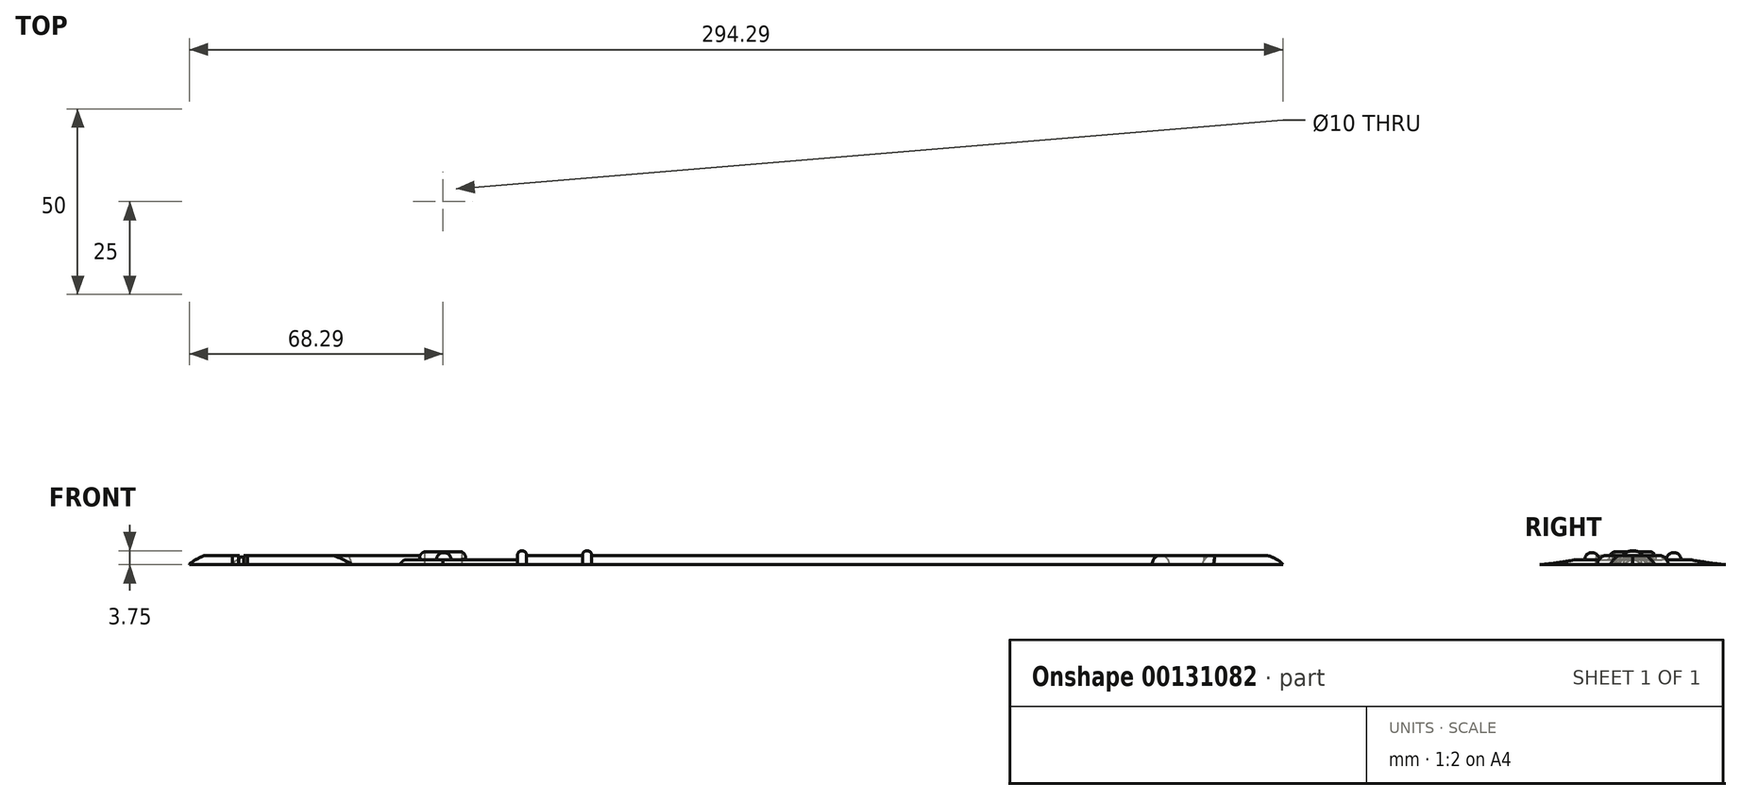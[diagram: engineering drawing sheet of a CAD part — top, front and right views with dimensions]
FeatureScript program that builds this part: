
annotation { "Feature Type Name" : "Feature", "Feature Type Description" : "" }
export const myFeature = defineFeature(function(context is Context, id is Id, definition is map)
    precondition{}
    {
        {
            var Q0;
            Q0=qCreatedBy(makeId("Front.planeOp"),FACE);
            var sketch = newSketch(context, id + "F0", { "sketchPlane" : qUnion([Q0])});
            skLineSegment(sketch, "E0", {"start": v(0, 0) * mm, "end": v(7, 0) * mm});
            skLineSegment(sketch, "E1", {"start": v(7, 0) * mm, "end": v(7, 2.5) * mm});
            skLineSegment(sketch, "E2", {"start": v(0, 0) * mm, "end": v(0, 7) * mm});
            skLineSegment(sketch, "E3", {"start": v(7, 0) * mm, "end": v(9.5, 0) * mm});
            skArc(sketch, "E4", {"start": v(9.5, 0) * mm, "mid": v(7, 2.5) * mm, "end": v(4.5, 0) * mm});
            skSolve(sketch);
        }
        {
            var Q0;
            Q0 = qSketchRegion(id + "F0", true);
            var Q1;
            Q1=sQuery(id+"F0.wireOp",EDGE,"E2");
            revolve(context, id + "F1", {"entities" : qUnion([Q0]), "axis" : qUnion([Q1]), "revolveType" : RevolveType.FULL});
        }
        {
            var Q0;
            Q0=qCreatedBy(makeId("Top.planeOp"),FACE);
            var sketch = newSketch(context, id + "F2", { "sketchPlane" : qUnion([Q0])});
            skLineSegment(sketch, "E5", {"start": v(0, 0) * mm, "end": v(-9, 0) * mm});
            skLineSegment(sketch, "E6", {"start": v(-9, 0) * mm, "end": v(26, 0) * mm});
            skLineSegment(sketch, "E7", {"start": v(4.75, 0) * mm, "end": v(26, 0) * mm});
            skArc(sketch, "E8", {"start": v(7.36, -6.07) * mm, "mid": v(7.17, -2.56) * mm, "end": v(4.75, 0) * mm});
            skArc(sketch, "E9", {"start": v(7.36, -6.07) * mm, "mid": v(17.19, -4.6) * mm, "end": v(26, 0) * mm});
            skArc(sketch, "E10", {"start": v(4.75, 0) * mm, "mid": v(7.07, 2.45) * mm, "end": v(7.36, 5.8) * mm});
            skArc(sketch, "E11", {"start": v(26, 0) * mm, "mid": v(17.17, 4.46) * mm, "end": v(7.36, 5.8) * mm});
            skSolve(sketch);
        }
        {
            var Q0;
            Q0 = qSketchRegion(id + "F2", true);
            extrude(context, id + "F3", {"entities" : qUnion([Q0]), "operationType" : NewBodyOperationType.ADD, "depth" : 2.5 * mm});
        }
        {
            var Q0;
            Q0=makeQuery(id+"F3.opExtrude","CAP_EDGE",EDGE,{"disambiguationData":[OSD([sQuery(id+"F2.wireOp",EDGE,"E9")])],"isStart":false});
            var Q1;
            Q1=makeQuery(id+"F3.opExtrude","CAP_EDGE",EDGE,{"disambiguationData":[OSD([sQuery(id+"F2.wireOp",EDGE,"E11")])],"isStart":false});
            fillet(context, id + "F4", {"entities" : qUnion([Q0, Q1]), "radius" : 2.5 * mm, "tangentPropagation" : true, "rho" : 0.18, "crossSection" : FilletCrossSection.CONIC, "allowEdgeOverflow" : false});
        }
        {
            var Q0;
            Q0=qCreatedBy(makeId("Right.planeOp"),FACE);
            var sketch = newSketch(context, id + "F5", { "sketchPlane" : qUnion([Q0])});
            skLineSegment(sketch, "E12", {"start": v(0, 0) * mm, "end": v(-2.5, 0) * mm});
            skLineSegment(sketch, "E13", {"start": v(-2.5, 0) * mm, "end": v(2.5, 0) * mm});
            skPoint(sketch, "E13.endSnap0", {"position": v(-1.25, 0) * mm});
            skArc(sketch, "E14", {"start": v(2.5, 0) * mm, "mid": v(0, 2.5) * mm, "end": v(-2.5, 0) * mm});
            skSolve(sketch);
        }
        {
            var Q0;
            {var subQ0=sQuery(id+"F5.wireOp",EDGE,"E14");Q0=makeQuery(id+"F5.imprint","IMPRINT",FACE,{"disambiguationData":[TD([[makeQuery(id+"F5.imprint","IMPRINT",EDGE,{"derivedFrom":subQ0}),1.0]])]});}
            var Q1;
            Q1=sQuery(id+"F5.wireOp",EDGE,"E13");
            var Q2;
            Q2=sQuery(id+"F5.wireOp",EDGE,"E14");
            extrude(context, id + "F6", {"entities" : qUnion([Q0]), "operationType" : NewBodyOperationType.ADD, "surfaceEntities" : qUnion([Q1, Q2]), "oppositeDirection" : true, "depth" : 160 * mm, "hasSecondDirection" : true, "secondDirectionOppositeDirection" : true, "secondDirectionDepth" : 7 * mm});
        }
        {
            var Q0;
            Q0=makeQuery(id+"F6.opExtrude","CAP_FACE",FACE,{"disambiguationData":[OSD([sQuery(id+"F5.wireOp",EDGE,"E13"),sQuery(id+"F5.wireOp",EDGE,"E14")])],"isStart":false});
            var sketch = newSketch(context, id + "F7", { "sketchPlane" : qUnion([Q0])});
            skLineSegment(sketch, "E15", {"start": v(0, 0) * mm, "end": v(3.75, 0) * mm});
            skLineSegment(sketch, "E16", {"start": v(3.75, 0) * mm, "end": v(-3.75, 0) * mm});
            skArc(sketch, "E17", {"start": v(3.75, 0) * mm, "mid": v(0, 3.75) * mm, "end": v(-3.75, 0) * mm});
            skSolve(sketch);
        }
        {
            var Q0;
            Q0 = qSketchRegion(id + "F7", true);
            extrude(context, id + "F8", {"entities" : qUnion([Q0]), "operationType" : NewBodyOperationType.ADD, "depth" : 2.5 * mm});
        }
        {
            var Q0;
            Q0=makeQuery(id+"F8.opExtrude","CAP_EDGE",EDGE,{"disambiguationData":[OSD([sQuery(id+"F7.wireOp",EDGE,"E17")])],"isStart":false});
            var Q1;
            Q1=makeQuery(id+"F8.opExtrude","CAP_EDGE",EDGE,{"disambiguationData":[OSD([sQuery(id+"F7.wireOp",EDGE,"E17")])],"isStart":true});
            fillet(context, id + "F9", {"entities" : qUnion([Q0, Q1]), "radius" : 1.25 * mm, "tangentPropagation" : true, "allowEdgeOverflow" : false});
        }
        {
            var Q0;
            Q0=makeQuery(id+"F8.opExtrude","CAP_FACE",FACE,{"disambiguationData":[OSD([sQuery(id+"F7.wireOp",EDGE,"E16"),sQuery(id+"F7.wireOp",EDGE,"E17")])],"isStart":false});
            var sketch = newSketch(context, id + "F10", { "sketchPlane" : qUnion([Q0])});
            skArc(sketch, "E18", {"start": v(2.5, 0) * mm, "mid": v(0, 2.5) * mm, "end": v(-2.5, 0) * mm});
            skSolve(sketch);
        }
        {
            var Q0;
            Q0 = qSketchRegion(id + "F10", true);
            var Q1;
            Q1=makeQuery(id+"F10.imprint","IMPRINT",FACE,{"disambiguationData":[TD([[makeQuery(id+"F10.imprint","IMPRINT",EDGE,{"derivedFrom":sQuery(id+"F10.wireOp",EDGE,"E18")}),1.0]])]});
            extrude(context, id + "F11", {"entities" : qUnion([Q0, Q1]), "operationType" : NewBodyOperationType.ADD, "depth" : 15 * mm});
        }
        {
            var Q0;
            Q0=makeQuery(id+"F11.opExtrude","CAP_FACE",FACE,{"disambiguationData":[OSD([sQuery(id+"F7.wireOp",EDGE,"E16"),sQuery(id+"F10.wireOp",EDGE,"E18")])],"isStart":false});
            var sketch = newSketch(context, id + "F12", { "sketchPlane" : qUnion([Q0])});
            skLineSegment(sketch, "E19", {"start": v(0, 0) * mm, "end": v(3.75, 0) * mm});
            skLineSegment(sketch, "E20", {"start": v(3.75, 0) * mm, "end": v(-3.75, 0) * mm});
            skArc(sketch, "E21", {"start": v(3.75, 0) * mm, "mid": v(0, 3.75) * mm, "end": v(-3.75, 0) * mm});
            skSolve(sketch);
        }
        {
            var Q0;
            Q0 = qSketchRegion(id + "F12", true);
            extrude(context, id + "F13", {"entities" : qUnion([Q0]), "operationType" : NewBodyOperationType.ADD, "depth" : 2.5 * mm});
        }
        {
            var Q0;
            Q0=makeQuery(id+"F13.opExtrude","CAP_EDGE",EDGE,{"disambiguationData":[OSD([sQuery(id+"F12.wireOp",EDGE,"E21")])],"isStart":false});
            var Q1;
            Q1=makeQuery(id+"F13.opExtrude","CAP_EDGE",EDGE,{"disambiguationData":[OSD([sQuery(id+"F12.wireOp",EDGE,"E21")])],"isStart":true});
            fillet(context, id + "F14", {"entities" : qUnion([Q0, Q1]), "radius" : 1.25 * mm, "tangentPropagation" : true, "allowEdgeOverflow" : false});
        }
        {
            var Q0;
            Q0=qCreatedBy(makeId("Top.planeOp"),FACE);
            var sketch = newSketch(context, id + "F15", { "sketchPlane" : qUnion([Q0])});
            skLineSegment(sketch, "E22", {"start": v(0, 0) * mm, "end": v(-180, 0) * mm});
            skLineSegment(sketch, "E23", {"start": v(-180, 0) * mm, "end": v(-180, -2.5) * mm});
            skLineSegment(sketch, "E24", {"start": v(-180, 0) * mm, "end": v(-180, 2.5) * mm});
            skLineSegment(sketch, "E25", {"start": v(-180, 0) * mm, "end": v(-200, 0) * mm});
            skLineSegment(sketch, "E26", {"start": v(-200, 0) * mm, "end": v(-200, 25) * mm});
            skLineSegment(sketch, "E27", {"start": v(-200, 0) * mm, "end": v(-200, -25) * mm});
            skCircle(sketch, "E28", {"center": v(-200, 0) * mm, "radius": 5 * mm});
            skCircle(sketch, "E29", {"center": v(-200.1, -0.08) * mm, "radius": 6.25 * mm});
            skArc(sketch, "E30", {"start": v(-200, 25) * mm, "mid": v(-193.97, 10.22) * mm, "end": v(-180, 2.5) * mm});
            skArc(sketch, "E31", {"start": v(-180, -2.5) * mm, "mid": v(-193.97, -10.22) * mm, "end": v(-200, -25) * mm});
            skLineSegment(sketch, "E32", {"start": v(-200, 0) * mm, "end": v(-224.5, 0) * mm});
            skArc(sketch, "E33", {"start": v(-200, -25) * mm, "mid": v(-207.53, -7.88) * mm, "end": v(-224.5, 0) * mm});
            skArc(sketch, "E34", {"start": v(-224.5, 0) * mm, "mid": v(-207.53, 7.88) * mm, "end": v(-200, 25) * mm});
            skLineSegment(sketch, "E35", {"start": v(-224.5, 0) * mm, "end": v(-224.5, -10) * mm});
            skLineSegment(sketch, "E36", {"start": v(-224.5, 0) * mm, "end": v(-224.5, 10) * mm});
            skLineSegment(sketch, "E37", {"start": v(-203.7, 3.36) * mm, "end": v(-203.7, -3.36) * mm});
            skArc(sketch, "E38", {"start": v(-224.5, 10) * mm, "mid": v(-214.57, 5.23) * mm, "end": v(-203.7, 3.36) * mm});
            skArc(sketch, "E39", {"start": v(-203.7, -3.36) * mm, "mid": v(-214.57, -5.23) * mm, "end": v(-224.5, -10) * mm});
            skLineSegment(sketch, "E40", {"start": v(-224.5, 0) * mm, "end": v(-268.3, 0) * mm});
            skArc(sketch, "E41", {"start": v(-224.5, 10) * mm, "mid": v(-246.87, 7.07) * mm, "end": v(-268.3, 0) * mm});
            skArc(sketch, "E42", {"start": v(-268.3, 0) * mm, "mid": v(-246.87, -7.07) * mm, "end": v(-224.5, -10) * mm});
            skArc(sketch, "E43", {"start": v(-255.35, -4.8) * mm, "mid": v(-254.8, 0) * mm, "end": v(-255.35, 4.8) * mm});
            skArc(sketch, "E44", {"start": v(-253.91, -5.23) * mm, "mid": v(-253.25, 0) * mm, "end": v(-253.91, 5.23) * mm});
            skArc(sketch, "E45", {"start": v(-256.64, 4.4) * mm, "mid": v(-254.14, 3.38) * mm, "end": v(-252.61, 5.6) * mm});
            skArc(sketch, "E46", {"start": v(-252.61, -5.6) * mm, "mid": v(-254.14, -3.38) * mm, "end": v(-256.64, -4.4) * mm});
            skSolve(sketch);
        }
        {
            var Q0;
            {var subQ1=sQuery(id+"F15.wireOp",EDGE,"E26");var subQ3=sQuery(id+"F15.wireOp",EDGE,"E29");var subQ4=makeQuery(id+"F15.imprint","INTERSECT",VERTEX,{"derivedFrom":[subQ1,subQ3]});Q0=makeQuery(id+"F15.imprint","IMPRINT",FACE,{"disambiguationData":[TD([[makeQuery(id+"F15.imprint","IMPRINT",EDGE,{"disambiguationData":[TD([[subQ4,-1.0]])],"derivedFrom":subQ3}),-1.0]])]});}
            var Q1;
            {var subQ5=sQuery(id+"F15.wireOp",EDGE,"E24");Q1=makeQuery(id+"F15.imprint","IMPRINT",FACE,{"disambiguationData":[TD([[makeQuery(id+"F15.imprint","IMPRINT",EDGE,{"derivedFrom":subQ5}),1.0]])]});}
            var Q2;
            {var subQ6=sQuery(id+"F15.wireOp",EDGE,"E23");Q2=makeQuery(id+"F15.imprint","IMPRINT",FACE,{"disambiguationData":[TD([[makeQuery(id+"F15.imprint","IMPRINT",EDGE,{"derivedFrom":subQ6}),-1.0]])]});}
            var Q3;
            {var subQ1=sQuery(id+"F15.wireOp",EDGE,"E27");var subQ3=sQuery(id+"F15.wireOp",EDGE,"E29");var subQ4=makeQuery(id+"F15.imprint","INTERSECT",VERTEX,{"derivedFrom":[subQ1,subQ3]});Q3=makeQuery(id+"F15.imprint","IMPRINT",FACE,{"disambiguationData":[TD([[makeQuery(id+"F15.imprint","IMPRINT",EDGE,{"disambiguationData":[TD([[subQ4,1.0]])],"derivedFrom":subQ3}),-1.0]])]});}
            extrude(context, id + "F16", {"entities" : qUnion([Q0, Q1, Q2, Q3]), "operationType" : NewBodyOperationType.ADD, "depth" : 1.25 * mm});
        }
        {
            var Q0;
            Q0=makeQuery(id+"F16.opExtrude","CAP_EDGE",EDGE,{"disambiguationData":[OSD([sQuery(id+"F15.wireOp",EDGE,"E31")])],"isStart":false});
            var Q1;
            Q1=makeQuery(id+"F16.opExtrude","CAP_EDGE",EDGE,{"disambiguationData":[OSD([sQuery(id+"F15.wireOp",EDGE,"E33")])],"isStart":false});
            var Q2;
            Q2=makeQuery(id+"F16.opExtrude","CAP_EDGE",EDGE,{"disambiguationData":[OSD([sQuery(id+"F15.wireOp",EDGE,"E34")])],"isStart":false});
            var Q3;
            Q3=makeQuery(id+"F16.opExtrude","CAP_EDGE",EDGE,{"disambiguationData":[OSD([sQuery(id+"F15.wireOp",EDGE,"E30")])],"isStart":false});
            fillet(context, id + "F17", {"entities" : qUnion([Q0, Q1, Q2, Q3]), "radius" : 2.5 * mm, "tangentPropagation" : true, "rho" : 0.18, "crossSection" : FilletCrossSection.CONIC, "allowEdgeOverflow" : false});
        }
        {
            var Q0;
            {var subQ0=sQuery(id+"F15.wireOp",EDGE,"E38");var subQ1=sQuery(id+"F15.wireOp",EDGE,"E29");var subQ2=makeQuery(id+"F15.imprint","INTERSECT",VERTEX,{"derivedFrom":[subQ1,subQ0]});Q0=makeQuery(id+"F15.imprint","IMPRINT",FACE,{"disambiguationData":[TD([[makeQuery(id+"F15.imprint","IMPRINT",EDGE,{"disambiguationData":[TD([[subQ2,-1.0]])],"derivedFrom":subQ1}),-1.0]])]});}
            var Q1;
            {var subQ0=sQuery(id+"F15.wireOp",EDGE,"E32");var subQ1=sQuery(id+"F15.wireOp",EDGE,"E29");var subQ2=makeQuery(id+"F15.imprint","INTERSECT",VERTEX,{"derivedFrom":[subQ1,subQ0]});Q1=makeQuery(id+"F15.imprint","IMPRINT",FACE,{"disambiguationData":[TD([[makeQuery(id+"F15.imprint","IMPRINT",EDGE,{"disambiguationData":[TD([[subQ2,-1.0]])],"derivedFrom":subQ1}),-1.0]])]});}
            var Q2;
            {var subQ0=sQuery(id+"F15.wireOp",EDGE,"E35");Q2=makeQuery(id+"F15.imprint","IMPRINT",FACE,{"disambiguationData":[TD([[makeQuery(id+"F15.imprint","IMPRINT",EDGE,{"derivedFrom":subQ0}),1.0]])]});}
            var Q3;
            {var subQ7=sQuery(id+"F15.wireOp",EDGE,"E35");Q3=makeQuery(id+"F15.imprint","IMPRINT",FACE,{"disambiguationData":[TD([[makeQuery(id+"F15.imprint","IMPRINT",EDGE,{"derivedFrom":subQ7}),-1.0]])]});}
            var Q4;
            {var subQ6=sQuery(id+"F15.wireOp",EDGE,"E36");Q4=makeQuery(id+"F15.imprint","IMPRINT",FACE,{"disambiguationData":[TD([[makeQuery(id+"F15.imprint","IMPRINT",EDGE,{"derivedFrom":subQ6}),1.0]])]});}
            var Q5;
            {var subQ1=sQuery(id+"F15.wireOp",EDGE,"E40");var subQ3=sQuery(id+"F15.wireOp",EDGE,"E43");var subQ4=makeQuery(id+"F15.imprint","INTERSECT",VERTEX,{"derivedFrom":[subQ1,subQ3]});Q5=makeQuery(id+"F15.imprint","IMPRINT",FACE,{"disambiguationData":[TD([[makeQuery(id+"F15.imprint","IMPRINT",EDGE,{"disambiguationData":[TD([[subQ4,1.0]])],"derivedFrom":subQ3}),1.0]])]});}
            var Q6;
            {var subQ1=sQuery(id+"F15.wireOp",EDGE,"E40");var subQ3=sQuery(id+"F15.wireOp",EDGE,"E43");var subQ4=makeQuery(id+"F15.imprint","INTERSECT",VERTEX,{"derivedFrom":[subQ1,subQ3]});Q6=makeQuery(id+"F15.imprint","IMPRINT",FACE,{"disambiguationData":[TD([[makeQuery(id+"F15.imprint","IMPRINT",EDGE,{"disambiguationData":[TD([[subQ4,-1.0]])],"derivedFrom":subQ3}),1.0]])]});}
            var Q7;
            {var subQ0=sQuery(id+"F15.wireOp",EDGE,"E36");Q7=makeQuery(id+"F15.imprint","IMPRINT",FACE,{"disambiguationData":[TD([[makeQuery(id+"F15.imprint","IMPRINT",EDGE,{"derivedFrom":subQ0}),-1.0]])]});}
            extrude(context, id + "F18", {"entities" : qUnion([Q0, Q1, Q2, Q3, Q4, Q5, Q6, Q7]), "operationType" : NewBodyOperationType.ADD, "depth" : 2.5 * mm});
        }
        {
            var Q0;
            {var subQ0=sQuery(id+"F15.wireOp",EDGE,"E42");Q0=makeQuery(id+"F18.opExtrude","CAP_EDGE",EDGE,{"disambiguationData":[OSD([subQ0]),TDD([makeQuery(id+"F15.imprint","IMPRINT",EDGE,{"disambiguationData":[TD([[makeQuery(id+"F15.imprint","INTERSECT",VERTEX,{"disambiguationData":[OD(1.0)],"derivedFrom":[subQ0,sQuery(id+"F15.wireOp",EDGE,"E46")]}),1.0]])],"derivedFrom":subQ0})])],"isStart":false});}
            var Q1;
            {var subQ0=sQuery(id+"F15.wireOp",EDGE,"E41");Q1=makeQuery(id+"F18.opExtrude","CAP_EDGE",EDGE,{"disambiguationData":[OSD([subQ0]),TDD([makeQuery(id+"F15.imprint","IMPRINT",EDGE,{"disambiguationData":[TD([[makeQuery(id+"F15.imprint","INTERSECT",VERTEX,{"disambiguationData":[OD(0.0)],"derivedFrom":[subQ0,sQuery(id+"F15.wireOp",EDGE,"E45")]}),-1.0]])],"derivedFrom":subQ0})])],"isStart":false});}
            var Q2;
            {var subQ0=sQuery(id+"F15.wireOp",EDGE,"E41");Q2=makeQuery(id+"F18.opExtrude","CAP_EDGE",EDGE,{"disambiguationData":[OSD([subQ0]),TDD([makeQuery(id+"F15.imprint","IMPRINT",EDGE,{"disambiguationData":[TD([[makeQuery(id+"F15.imprint","INTERSECT",VERTEX,{"disambiguationData":[OD(1.0)],"derivedFrom":[subQ0,sQuery(id+"F15.wireOp",EDGE,"E45")]}),1.0]])],"derivedFrom":subQ0})])],"isStart":false});}
            var Q3;
            {var subQ0=sQuery(id+"F15.wireOp",EDGE,"E42");Q3=makeQuery(id+"F18.opExtrude","CAP_EDGE",EDGE,{"disambiguationData":[OSD([subQ0]),TDD([makeQuery(id+"F15.imprint","IMPRINT",EDGE,{"disambiguationData":[TD([[makeQuery(id+"F15.imprint","INTERSECT",VERTEX,{"disambiguationData":[OD(0.0)],"derivedFrom":[subQ0,sQuery(id+"F15.wireOp",EDGE,"E46")]}),-1.0]])],"derivedFrom":subQ0})])],"isStart":false});}
            var Q4;
            Q4=makeQuery(id+"F18.opExtrude","CAP_EDGE",EDGE,{"disambiguationData":[OSD([sQuery(id+"F15.wireOp",EDGE,"E39")])],"isStart":false});
            var Q5;
            Q5=makeQuery(id+"F18.opExtrude","CAP_EDGE",EDGE,{"disambiguationData":[OSD([sQuery(id+"F15.wireOp",EDGE,"E38")])],"isStart":false});
            fillet(context, id + "F19", {"entities" : qUnion([Q0, Q1, Q2, Q3, Q4, Q5]), "radius" : 3.7 * mm, "tangentPropagation" : true, "rho" : 0.18, "crossSection" : FilletCrossSection.CONIC, "allowEdgeOverflow" : false});
        }
        {
            var Q0;
            {var subQ0=sQuery(id+"F15.wireOp",EDGE,"E44");var subQ1=sQuery(id+"F15.wireOp",EDGE,"E40");var subQ2=makeQuery(id+"F15.imprint","INTERSECT",VERTEX,{"derivedFrom":[subQ1,subQ0]});Q0=makeQuery(id+"F15.imprint","IMPRINT",FACE,{"disambiguationData":[TD([[makeQuery(id+"F15.imprint","IMPRINT",EDGE,{"disambiguationData":[TD([[subQ2,-1.0]])],"derivedFrom":subQ1}),-1.0]])]});}
            var Q1;
            {var subQ0=sQuery(id+"F15.wireOp",EDGE,"E44");var subQ1=sQuery(id+"F15.wireOp",EDGE,"E40");var subQ2=makeQuery(id+"F15.imprint","INTERSECT",VERTEX,{"derivedFrom":[subQ1,subQ0]});Q1=makeQuery(id+"F15.imprint","IMPRINT",FACE,{"disambiguationData":[TD([[makeQuery(id+"F15.imprint","IMPRINT",EDGE,{"disambiguationData":[TD([[subQ2,-1.0]])],"derivedFrom":subQ1}),1.0]])]});}
            extrude(context, id + "F20", {"entities" : qUnion([Q0, Q1]), "depth" : 2 * mm});
        }
        {
            var Q0;
            Q0=makeQuery(id+"F20.opExtrude","CAP_EDGE",EDGE,{"disambiguationData":[OSD([sQuery(id+"F15.wireOp",EDGE,"E46")])],"isStart":false});
            var Q1;
            Q1=makeQuery(id+"F20.opExtrude","CAP_EDGE",EDGE,{"disambiguationData":[OSD([sQuery(id+"F15.wireOp",EDGE,"E45")])],"isStart":false});
            fillet(context, id + "F21", {"entities" : qUnion([Q0, Q1]), "radius" : 1.29 * mm, "tangentPropagation" : true, "rho" : 0.05, "crossSection" : FilletCrossSection.CONIC, "allowEdgeOverflow" : false});
        }
        {
            var Q0;
            {var subQ0=sQuery(id+"F15.wireOp",EDGE,"E28");var subQ1=sQuery(id+"F15.wireOp",EDGE,"E26");var subQ2=makeQuery(id+"F15.imprint","INTERSECT",VERTEX,{"derivedFrom":[subQ1,subQ0]});Q0=makeQuery(id+"F15.imprint","IMPRINT",FACE,{"disambiguationData":[TD([[makeQuery(id+"F15.imprint","IMPRINT",EDGE,{"disambiguationData":[TD([[subQ2,-1.0]])],"derivedFrom":subQ1}),1.0]])]});}
            var Q1;
            {var subQ0=sQuery(id+"F15.wireOp",EDGE,"E38");var subQ5=sQuery(id+"F15.wireOp",EDGE,"E29");var subQ6=makeQuery(id+"F15.imprint","INTERSECT",VERTEX,{"derivedFrom":[subQ5,subQ0]});Q1=makeQuery(id+"F15.imprint","IMPRINT",FACE,{"disambiguationData":[TD([[makeQuery(id+"F15.imprint","IMPRINT",EDGE,{"disambiguationData":[TD([[subQ6,-1.0]])],"derivedFrom":subQ5}),1.0]])]});}
            var Q2;
            {var subQ3=sQuery(id+"F15.wireOp",EDGE,"E32");var subQ5=sQuery(id+"F15.wireOp",EDGE,"E29");var subQ6=makeQuery(id+"F15.imprint","INTERSECT",VERTEX,{"derivedFrom":[subQ5,subQ3]});Q2=makeQuery(id+"F15.imprint","IMPRINT",FACE,{"disambiguationData":[TD([[makeQuery(id+"F15.imprint","IMPRINT",EDGE,{"disambiguationData":[TD([[subQ6,-1.0]])],"derivedFrom":subQ5}),1.0]])]});}
            var Q3;
            {var subQ0=sQuery(id+"F15.wireOp",EDGE,"E28");var subQ1=sQuery(id+"F15.wireOp",EDGE,"E27");var subQ2=makeQuery(id+"F15.imprint","INTERSECT",VERTEX,{"derivedFrom":[subQ1,subQ0]});Q3=makeQuery(id+"F15.imprint","IMPRINT",FACE,{"disambiguationData":[TD([[makeQuery(id+"F15.imprint","IMPRINT",EDGE,{"disambiguationData":[TD([[subQ2,-1.0]])],"derivedFrom":subQ1}),-1.0]])]});}
            var Q4;
            {var subQ0=sQuery(id+"F15.wireOp",EDGE,"E29");var subQ1=sQuery(id+"F15.wireOp",EDGE,"E25");var subQ2=makeQuery(id+"F15.imprint","INTERSECT",VERTEX,{"derivedFrom":[subQ1,subQ0]});Q4=makeQuery(id+"F15.imprint","IMPRINT",FACE,{"disambiguationData":[TD([[makeQuery(id+"F15.imprint","IMPRINT",EDGE,{"disambiguationData":[TD([[subQ2,-1.0]])],"derivedFrom":subQ1}),1.0]])]});}
            var Q5;
            {var subQ0=sQuery(id+"F15.wireOp",EDGE,"E29");var subQ1=sQuery(id+"F15.wireOp",EDGE,"E25");var subQ2=makeQuery(id+"F15.imprint","INTERSECT",VERTEX,{"derivedFrom":[subQ1,subQ0]});Q5=makeQuery(id+"F15.imprint","IMPRINT",FACE,{"disambiguationData":[TD([[makeQuery(id+"F15.imprint","IMPRINT",EDGE,{"disambiguationData":[TD([[subQ2,-1.0]])],"derivedFrom":subQ1}),-1.0]])]});}
            extrude(context, id + "F22", {"entities" : qUnion([Q0, Q1, Q2, Q3, Q4, Q5]), "operationType" : NewBodyOperationType.ADD, "depth" : 3.5 * mm});
        }
        {
            var Q0;
            Q0=makeQuery(id+"F22.opExtrude","CAP_EDGE",EDGE,{"disambiguationData":[OSD([sQuery(id+"F15.wireOp",EDGE,"E29")])],"isStart":false});
            fillet(context, id + "F23", {"entities" : qUnion([Q0]), "radius" : 2.5 * mm, "tangentPropagation" : true, "rho" : 0.6, "crossSection" : FilletCrossSection.CONIC, "allowEdgeOverflow" : false});
        }
        {
            var Q0;
            Q0=makeQuery(id+"F16.opExtrude","CAP_FACE",FACE,{"disambiguationData":[OSD([sQuery(id+"F15.wireOp",EDGE,"E23"),sQuery(id+"F15.wireOp",EDGE,"E24"),sQuery(id+"F15.wireOp",EDGE,"E29"),sQuery(id+"F15.wireOp",EDGE,"E30"),sQuery(id+"F15.wireOp",EDGE,"E31"),sQuery(id+"F15.wireOp",EDGE,"E33"),sQuery(id+"F15.wireOp",EDGE,"E34"),sQuery(id+"F15.wireOp",EDGE,"E38"),sQuery(id+"F15.wireOp",EDGE,"E39")])],"isStart":false});
            var sketch = newSketch(context, id + "F24", { "sketchPlane" : qUnion([Q0])});
            skLineSegment(sketch, "E47", {"start": v(0, 0) * mm, "end": v(-199.8, 0) * mm});
            skLineSegment(sketch, "E48", {"start": v(-199.8, 0) * mm, "end": v(-199.8, 11) * mm});
            skLineSegment(sketch, "E49", {"start": v(-199.8, 0) * mm, "end": v(-199.8, -11) * mm});
            skCircle(sketch, "E50", {"center": v(-199.8, 11) * mm, "radius": 2 * mm});
            skCircle(sketch, "E51", {"center": v(-199.8, -11) * mm, "radius": 2 * mm});
            skSolve(sketch);
        }
        {
            var Q0;
            Q0 = qSketchRegion(id + "F24", true);
            extrude(context, id + "F25", {"entities" : qUnion([Q0]), "operationType" : NewBodyOperationType.ADD, "depth" : 2 * mm});
        }
        {
            var Q0;
            Q0=makeQuery(id+"F25.opExtrude","CAP_EDGE",EDGE,{"disambiguationData":[OSD([sQuery(id+"F24.wireOp",EDGE,"E50")])],"isStart":false});
            var Q1;
            Q1=makeQuery(id+"F25.opExtrude","CAP_EDGE",EDGE,{"disambiguationData":[OSD([sQuery(id+"F24.wireOp",EDGE,"E51")])],"isStart":false});
            fillet(context, id + "F26", {"entities" : qUnion([Q0, Q1]), "radius" : 2 * mm, "tangentPropagation" : true, "allowEdgeOverflow" : false});
        }
    });
